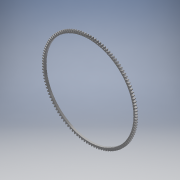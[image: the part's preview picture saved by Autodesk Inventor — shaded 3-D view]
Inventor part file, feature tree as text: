
AUTODESK INVENTOR PART (.ipt)
format: ipt  version: 2017 (Build 210142000, 142)  size: 621,056 bytes
history: native  units: mm (DEFAULTED — no unit token found)
features: plane x3, other x3, sketch x3, extrude x2
ambient origin geometry x8: Origin, YZ Plane, XZ Plane, XY Plane, X Axis, Y Axis, Z Axis, Center Point
bodies: Solid1 (feature_tree)
feature tree (11):
  extrude  "Extrusion1"  Depth=6.35mm TaperAngle=0.0deg
  plane  "Work Plane1"
  plane  "Work Plane2"
  plane  "Work Plane3"
  other  "Spur Gear"
  extrude  "Extrusion2"  Depth=76.2mm TaperAngle=0.0deg
  sketch  "Sketch1"  dims[d0=309.88mm d1=6.35mm d2=0.0mm]
  sketch  "Sketch2"  dims[d3=304.8mm d4=76.2mm d5=0.0mm]
  other  "Srf1"
  sketch  "Sketch3"  dims[d6=0.0mm d7=0.261799mm d9=0.0mm d14=0.0mm d15=175.26mm d16=0.0mm d17=0.0mm d18=0.0mm d19=175.26mm d20=292.1mm d21=25.4mm d22=0.0mm]
  other  "Pitch Diameter"
